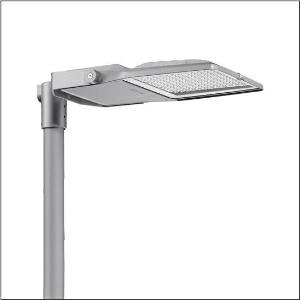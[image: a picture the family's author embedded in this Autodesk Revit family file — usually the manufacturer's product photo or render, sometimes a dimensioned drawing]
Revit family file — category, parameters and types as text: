
# Revit family: floodlight_fl_21_midi___pl33t_5xa7785f2f3a_cf02
name_source: partatom
category: Lighting Fixtures
units: mm (PartAtom-declared; Revit-internal decimal feet)

## family parameters
Cut with Voids When Loaded = No
Host = Face
Light Source = No
Part Type = Normal
Room Calculation Point = No
Round Connector Dimension = Use Diameter
Shared = No

## types (1)
- --- (1 x LED, 35340 lm, 271.6 W, 3000K)
    Apparent Load = 272 VA
    CIE Flux Codes = 26 75 99 100 100
    Color Rendering = 70
    Color Temperature = 3000K
    Default Elevation = 1800 mm
    Description = Floodlight FL 21 midi, floodlight, primary light control with lens, of PMMA, primary optical cover: protective disc, of toughened safety glass, transparent, light distribution: PL33T, light emission: direct distribution, installation type: surface-mounted, LED, High Power LED, rated luminous flux: 35.340lm, luminous efficacy: 130lm/W, light colour: 730, colour temperature: 3000K, control gear: ECG Smart Interface, control: flexible luminous flux parameterisation, time-dependent luminous flux control, constant luminous flux control, overheat protection, presetting dimming logarithmic, with terminal, 6-pole, mains connection: 220..240V, AC, 50/60Hz, start of lifetime: 272W, end of service life: 287W, reduction: 123W, luminaire housing, of diecast aluminium, powder-coated, Siteco® metallic grey (DB 702S), sealing non-destructively replaceable, please order mast flange separately, mast bracket, of steel, galvanised, powder-coated, Siteco® metallic grey (DB 702S), Smart Interface above, protection rating (complete): IP66, insulation class (complete): insulation class II (safety insulation), certification: CE, protection symbol: D, impact resistance: IK08, permissible operating ambient temperature: -40..+40°C, permissible operating ambient temperature for outdoor applications: -40..+50°C, standard: DIN EN 12944, LABS conformity tested according to VDMA 24364:2018-05, packaging unit: 1 piece

Light Distribution: PL33T
    Height = 76 mm
    Lamp = 1 x LED
    Lamp Light Flux = 35340 lm
    Lamp Power = 271.6 W
    Lamp count = 1
    Length = 657 mm
    Luminous efficacy = 130 lm/W
    Manufacturer = Siteco
    ModVariant = No
    Model = 5XA7785F2F3A
    Number of Poles = 1
    OnlyDefault = Yes
    Power Factor = 1
    Product Name = Floodlight FL 21 midi | PL33T
    Product group = floodlight | pylon annexe
    ProductGroupID = 6200
    Protection Class = Protection class II
    Protection Degree = IP 66
    RLX_Detail_Level = 1
    RLX_Emergency_Light_Flux = 0 lm
    RLX_Emergency_Type = 0
    RLX_Emergency_Type_DB = No
    RlxData = <blob elided: 153489 chars, md5=6b2e5a0c>
    Socket = socket
    Standby Power = 0 W
    System Light Flux = 35340 lm
    System Power = 272 W
    Type Comments = factory setting: luminous flux: 100 % | dim-lin: 254 | 620 mA
    Type Image = l_1007123.jpg
    URL = http://relux.com
    VarID = @adj_100625
    Voltage = 0 V
    Weight = 0.00 kg
    Width = 442 mm

## geometry (parser evidence)
native form markers: Blend x4, Sweep x11
no freeform markers — native parametric forms only
